# Revit family: 94538512
name_source: partatom
category: Modelos genéricos
revit_build: Autodesk Revit 2016 (Build: 20150220_1215(x64)
units: mm (PartAtom-declared; Revit-internal decimal feet)

## family parameters
Com base no plano de trabalho = Não
Compartilhado = Não
Corte com vazios quando carregados = Não
Cota do conector redondo = Utilizar diâmetro
Pode hospedar o vergalhão = Não
Ponto de cálculo do ambiente = Não
Sempre na vertical = Sim
Tipo de parte = Normal

## types (1)
- Lixeira Brasil Plus - 9453812
    Acabamento = Scotch brite
    Capacidade = 12 L
    Código de montagem = Lixeira Brasil Plus - 9453812
    Descrição = Lixeira Brasil Plus - 9453812
    Desenvolvedor = Factory Cursos & Desenvolvimento
    Espessura = 0,4 mm
    Fabricante = Tramontina
    Material = Aço Inox AISI 430
    Referencia = Lixeira Brasil Plus - 9453812
    Site do desenvolvedor = www.factorycursos.com.br
    Tampa = Sim
    Tipo de imagem = <Nenhum>
    Tratamento anti digitais = Não
    URL = www.tramontina.com.br
